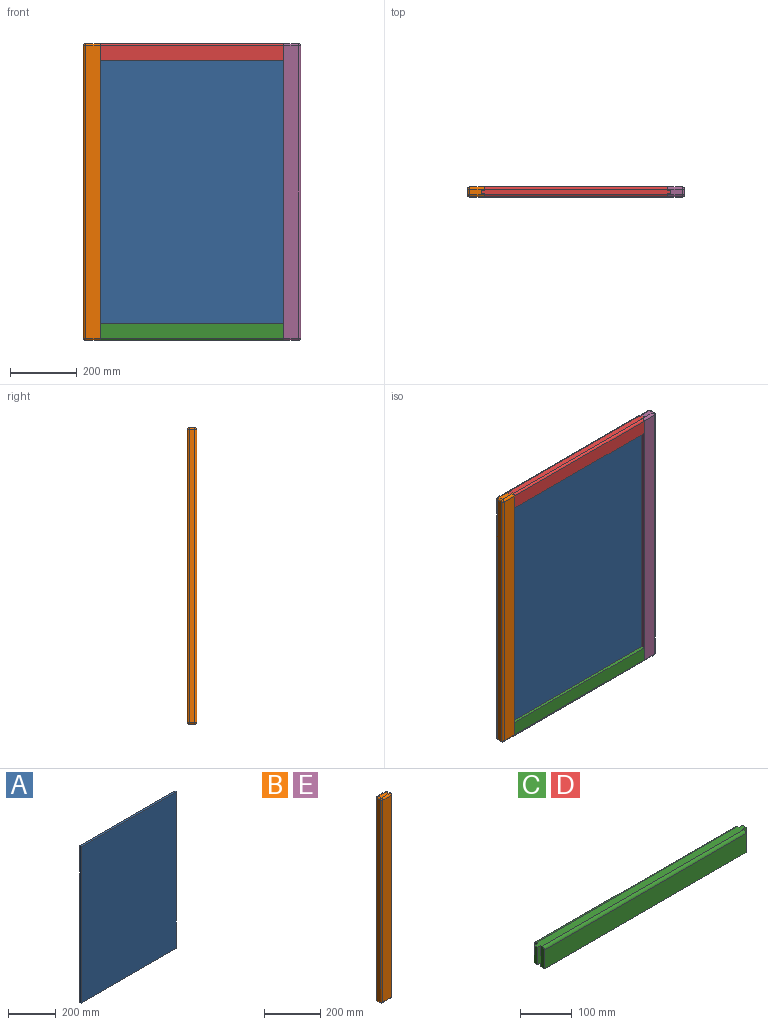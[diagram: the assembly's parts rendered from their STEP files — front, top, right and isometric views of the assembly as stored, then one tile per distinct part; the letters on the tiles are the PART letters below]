
ASSEMBLY  parts=5 mates=6
PART A: 6 faces, bbox 565.2x8.3x803.3 mm
  f0: plane 803.28x8.26mm, normal (1,0,0), area 6631mm2, adj f1,f3,f4,f5
  f1: plane 565.15x8.26mm, normal (0,0,1), area 4665.3mm2, adj f0,f2,f4,f5
  f2: plane 803.28x8.26mm, normal (-1,0,0), area 6631mm2, adj f1,f3,f4,f5
  f3: plane 565.15x8.26mm, normal (0,0,-1), area 4665.3mm2, adj f0,f2,f4,f5
  f4: plane 803.28x565.15mm, normal (0,-1,0), area 453970.9mm2, adj f0,f1,f2,f3
  f5: plane 803.28x565.15mm, normal (0,1,0), area 453970.9mm2, adj f0,f1,f2,f3
PART B: 22 faces, bbox 50.8x28.6x889 mm
  f0: plane 876.3x44.45mm, normal (0,-1,0), area 38951.5mm2, adj f1,f10,f11,f12
  f1: plane 889x9.53mm, normal (1,0,0), area 8450.4mm2, adj f0,f2,f8,f9,f10,f12
  f2: plane 889x9.53mm, normal (0,1,0), area 8467.7mm2, adj f1,f3,f8,f9
  f3: plane 889x9.53mm, normal (1,0,0), area 8467.7mm2, adj f2,f4,f8,f9
  f4: plane 889x9.53mm, normal (0,-1,0), area 8467.7mm2, adj f3,f5,f8,f9
  f5: plane 889x9.53mm, normal (1,0,0), area 8450.4mm2, adj f4,f6,f8,f9,f15,f18
  f6: plane 876.3x44.45mm, normal (0,1,0), area 38951.5mm2, adj f5,f15,f18,f21
  f7: plane 876.3x15.88mm, normal (-1,0,0), area 13911.3mm2, adj f11,f16,f17,f21
  f8: plane 44.45x15.88mm, normal (0,0,1), area 614.9mm2, adj f1,f2,f3,f4,f5,f10,f15,f16
  f9: plane 44.45x15.88mm, normal (0,0,-1), area 614.9mm2, adj f1,f2,f3,f4,f5,f12,f17,f18
  f10: cylinder r=6.35mm len=44.45mm, axis (-1,0,0), area 443.4mm2, adj f0,f1,f8,f13
  f11: cylinder r=6.35mm len=876.3mm, axis (0,0,-1), area 8740.7mm2, adj f0,f7,f13,f14
  f12: cylinder r=6.35mm len=44.45mm, axis (1,0,0), area 443.4mm2, adj f0,f1,f9,f14
  f13: sphere r=6.35mm, area 63.3mm2, adj f10,f11,f16
  f14: sphere r=6.35mm, area 63.3mm2, adj f11,f12,f17
  f15: cylinder r=6.35mm len=44.45mm, axis (1,0,0), area 443.4mm2, adj f5,f6,f8,f19
  f16: cylinder r=6.35mm len=15.88mm, axis (0,1,0), area 158.3mm2, adj f7,f8,f13,f19
  f17: cylinder r=6.35mm len=15.88mm, axis (0,-1,0), area 158.3mm2, adj f7,f9,f14,f20
  f18: cylinder r=6.35mm len=44.45mm, axis (-1,0,0), area 443.4mm2, adj f5,f6,f9,f20
  f19: sphere r=6.35mm, area 63.3mm2, adj f15,f16,f21
  f20: sphere r=6.35mm, area 63.3mm2, adj f17,f18,f21
  f21: cylinder r=6.35mm len=876.3mm, axis (0,0,1), area 8740.7mm2, adj f6,f7,f19,f20
PART C: 20 faces, bbox 568.3x28.6x50.8 mm
  f0: plane 549.28x44.45mm, normal (0,-1,0), area 24415.3mm2, adj f1,f13,f15,f19
  f1: plane 549.28x9.53mm, normal (0,0,-1), area 5231.8mm2, adj f0,f2,f13,f15
  f2: plane 549.28x9.53mm, normal (0,1,0), area 5231.8mm2, adj f1,f9,f13,f15
  f3: plane 549.28x9.53mm, normal (0,-1,0), area 5231.8mm2, adj f4,f9,f11,f17
  f4: plane 549.28x9.53mm, normal (0,0,-1), area 5231.8mm2, adj f3,f5,f11,f17
  f5: plane 549.28x44.45mm, normal (0,1,0), area 24415.3mm2, adj f4,f11,f17,f18
  f6: plane 568.33x15.88mm, normal (0,0,1), area 8901.2mm2, adj f7,f8,f10,f11,f12,f13,f14,f15
  f7: plane 41.28x9.53mm, normal (1,0,0), area 393.1mm2, adj f6,f9,f14,f16
  f8: plane 41.28x9.53mm, normal (-1,0,0), area 393.1mm2, adj f6,f9,f10,f12
  f9: plane 568.33x9.53mm, normal (0,0,-1), area 5413.3mm2, adj f2,f3,f7,f8,f10,f12,f14,f16
  f10: plane 41.28x9.53mm, normal (0,1,0), area 393.1mm2, adj f6,f8,f9,f11
  f11: plane 50.8x9.53mm, normal (-1,0,0), area 475.2mm2, adj f3,f4,f5,f6,f10,f18
  f12: plane 41.28x9.53mm, normal (0,-1,0), area 393.1mm2, adj f6,f8,f9,f13
  f13: plane 50.8x9.53mm, normal (-1,0,0), area 475.2mm2, adj f0,f1,f2,f6,f12,f19
  f14: plane 41.28x9.53mm, normal (0,-1,0), area 393.1mm2, adj f6,f7,f9,f15
  f15: plane 50.8x9.53mm, normal (1,0,0), area 475.2mm2, adj f0,f1,f2,f6,f14,f19
  f16: plane 41.28x9.53mm, normal (0,1,0), area 393.1mm2, adj f6,f7,f9,f17
  f17: plane 50.8x9.53mm, normal (1,0,0), area 475.2mm2, adj f3,f4,f5,f6,f16,f18
  f18: cylinder r=6.35mm len=549.28mm, axis (-1,0,0), area 5478.8mm2, adj f5,f6,f11,f17
  f19: cylinder r=6.35mm len=549.28mm, axis (-1,0,0), area 5478.8mm2, adj f0,f6,f13,f15
PART D: same geometry as C
PART E: same geometry as B
PLACE A rot(axis=(-0.06,1,0.03),0deg) t=(-52.85,224.76,369.3)mm
PLACE B t=(-325.9,206.98,-76.78)mm
PLACE C rot(axis=(0,-1,0),180deg) t=(232.9,206.98,-25.98)mm
PLACE D rot(axis=(0,1,0),0deg) t=(-335.43,206.98,761.42)mm
PLACE E rot(axis=(0,-1,0),180deg) t=(223.37,206.98,812.22)mm
MATE planar A.f2 <-> B.f3  axis (-1,0,0) through (-335.43,220.63,369.3)mm
MATE fastened C.f6 <-> B.f9  axis (0,0,-1) through (-335.43,216.5,-76.78)mm
MATE planar C.f2 <-> A.f4  axis (0,1,0) through (-51.26,216.5,-30.75)mm
MATE fastened D.f6 <-> E.f9  axis (0,0,1) through (232.9,216.5,812.22)mm
MATE fastened D.f6 <-> B.f8  axis (0,0,1) through (-335.43,216.5,812.22)mm
MATE planar A.f1 <-> D.f9  axis (0,0,1) through (-52.85,220.63,770.94)mm
